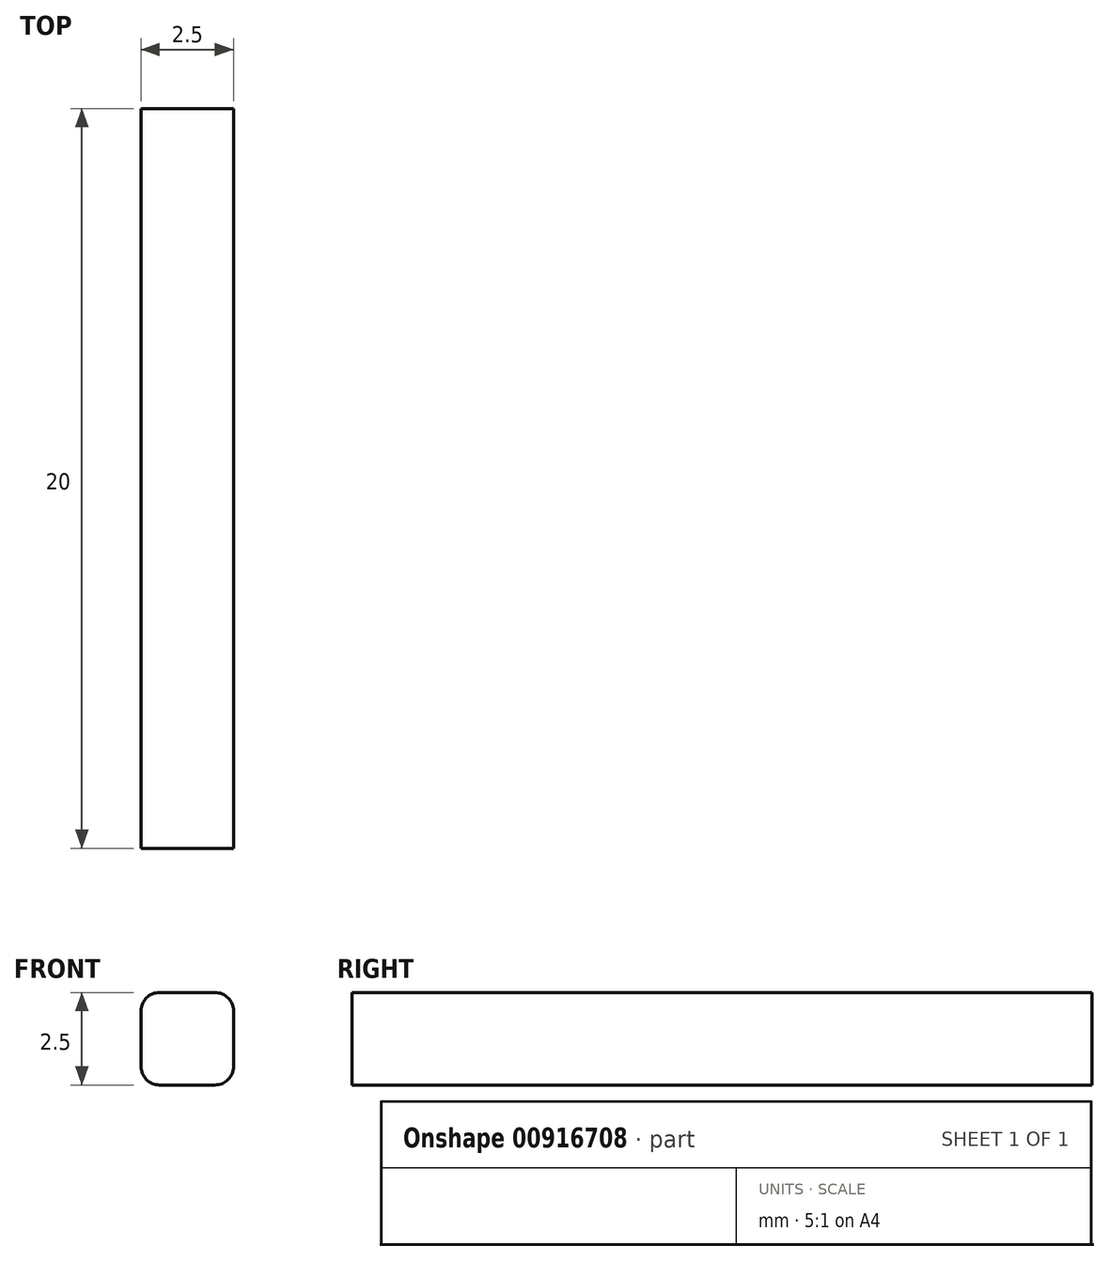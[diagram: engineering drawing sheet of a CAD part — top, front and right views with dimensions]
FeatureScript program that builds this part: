
annotation { "Feature Type Name" : "Feature", "Feature Type Description" : "" }
export const myFeature = defineFeature(function(context is Context, id is Id, definition is map)
    precondition{}
    {
        {
            var Q0;
            Q0=qCreatedBy(makeId("Front.planeOp"),FACE);
            var sketch = newSketch(context, id + "F0", { "sketchPlane" : qUnion([Q0])});
            skLineSegment(sketch, "E0.bottom", {"start": v(1.25, 1.25) * mm, "end": v(-1.25, 1.25) * mm});
            skLineSegment(sketch, "E0.top", {"start": v(1.25, -1.25) * mm, "end": v(-1.25, -1.25) * mm});
            skLineSegment(sketch, "E0.left", {"start": v(1.25, 1.25) * mm, "end": v(1.25, -1.25) * mm});
            skLineSegment(sketch, "E0.right", {"start": v(-1.25, 1.25) * mm, "end": v(-1.25, -1.25) * mm});
            skPoint(sketch, "E0.middle", {"position": v(0, 0) * mm});
            skSolve(sketch);
        }
        {
            var Q0;
            Q0=qCreatedBy(makeId("Top.planeOp"),FACE);
            var sketch = newSketch(context, id + "F1", { "sketchPlane" : qUnion([Q0])});
            skLineSegment(sketch, "E1", {"start": v(0, 0) * mm, "end": v(0, 20) * mm});
            skSolve(sketch);
        }
        {
            var Q0;
            Q0 = qSketchRegion(id + "F0", true);
            var Q1;
            Q1 = qConstructionFilter(qBodyType(qCreatedBy(id + "F1" ,EDGE), BodyType.WIRE), ConstructionObject.NO);
            sweep(context, id + "F2", {"profiles" : qUnion([Q0]), "path" : qUnion([Q1])});
        }
        {
            var Q0;
            Q0=makeQuery(id+"F2.opSweep","SWEPT_EDGE",EDGE,{"disambiguationData":[OSD([sQuery(id+"F0.wireOp",EDGE,"E0.top"),sQuery(id+"F0.wireOp",EDGE,"E0.right"),sQuery(id+"F1.wireOp",EDGE,"E1")])]});
            var Q1;
            Q1=makeQuery(id+"F2.opSweep","SWEPT_EDGE",EDGE,{"disambiguationData":[OSD([sQuery(id+"F0.wireOp",EDGE,"E0.bottom"),sQuery(id+"F0.wireOp",EDGE,"E0.right"),sQuery(id+"F1.wireOp",EDGE,"E1")])]});
            var Q2;
            Q2=makeQuery(id+"F2.opSweep","SWEPT_EDGE",EDGE,{"disambiguationData":[OSD([sQuery(id+"F0.wireOp",EDGE,"E0.bottom"),sQuery(id+"F0.wireOp",EDGE,"E0.left"),sQuery(id+"F1.wireOp",EDGE,"E1")])]});
            var Q3;
            Q3=makeQuery(id+"F2.opSweep","SWEPT_EDGE",EDGE,{"disambiguationData":[OSD([sQuery(id+"F0.wireOp",EDGE,"E0.top"),sQuery(id+"F0.wireOp",EDGE,"E0.left"),sQuery(id+"F1.wireOp",EDGE,"E1")])]});
            fillet(context, id + "F3", {"entities" : qUnion([Q0, Q1, Q2, Q3]), "radius" : 0.5 * mm, "tangentPropagation" : true, "allowEdgeOverflow" : false});
        }
    });
